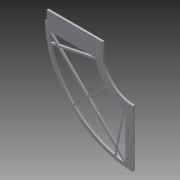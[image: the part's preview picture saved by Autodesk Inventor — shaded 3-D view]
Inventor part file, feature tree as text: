
AUTODESK INVENTOR PART (.ipt)
format: ipt  version: 2013 (Build 170138000, 138)  size: 2,576,896 bytes
history: native  units: mm (DEFAULTED — no unit token found)
features: sketch x8, extrude x7, reference x5, plane x3, other x3
ambient origin geometry x8: Origin, YZ Plane, XZ Plane, XY Plane, X Axis, Y Axis, Z Axis, Center Point
bodies: Solid1 (feature_tree)
feature tree (26):
  extrude  "Extrusion1"  Depth=6.35mm TaperAngle=0.0deg
  plane  "Work Plane1"
  plane  "Work Plane2"
  plane  "Work Plane3"
  other  "Spur Gear"
  extrude  "Extrusion2"  Depth=76.2mm TaperAngle=0.0deg
  extrude  "Extrusion3"  TaperAngle=0.0deg  [1 undecoded]
  extrude  "Extrusion4"  TaperAngle=0.0deg  [1 undecoded]
  extrude  "Extrusion5"  Depth=203.2mm
  extrude  "Extrusion7"  Depth=25.4mm TaperAngle=0.0deg
  extrude  "Extrusion8"  Depth=25.4mm
  sketch  "Sketch1"  dims[d0=582.77125mm d1=6.35mm d2=0.0mm]
  sketch  "Sketch2"  dims[d3=580.39mm d4=76.2mm d5=0.0mm]
  other  "Srf1"
  sketch  "Sketch3"  dims[d6=0.0mm d7=0.068744mm d9=0.0mm]
  sketch  "Sketch4"  dims[d14=0.0mm d15=304.8mm d16=0.0mm]
  sketch  "Sketch5"  dims[d17=0.0mm d18=0.0mm d19=304.8mm d21=203.2mm]
  sketch  "Sketch6"  dims[d22=25.4mm d23=0.0mm d24=25.4mm d25=0.0mm]
  sketch  "Sketch8"  dims[d26=254.0mm d29=25.4mm d30=25.4mm]
  reference  "Reference6"
  sketch  "Sketch10"  dims[d31=558.8mm d32=25.4mm d33=0.0mm d36=31.75mm d37=31.75mm d38=184.15mm d39=6.35mm d40=0.0mm d45=0.0mm d46=6.35mm d52=6.35mm d60=6.35mm d61=6.35mm d62=0.0mm d63=90.0deg d64=90.0deg d65=25.4mm d66=0.0mm]
  reference  "Reference7"
  reference  "Reference8"
  reference  "Reference9"
  reference  "Reference10"
  other  "Pitch Diameter"
note: 2 required parameter values undecoded (feature->parameter linkage not recoverable at this tier; creation-order binding heuristic only, values carry confidence <= 0.55)
